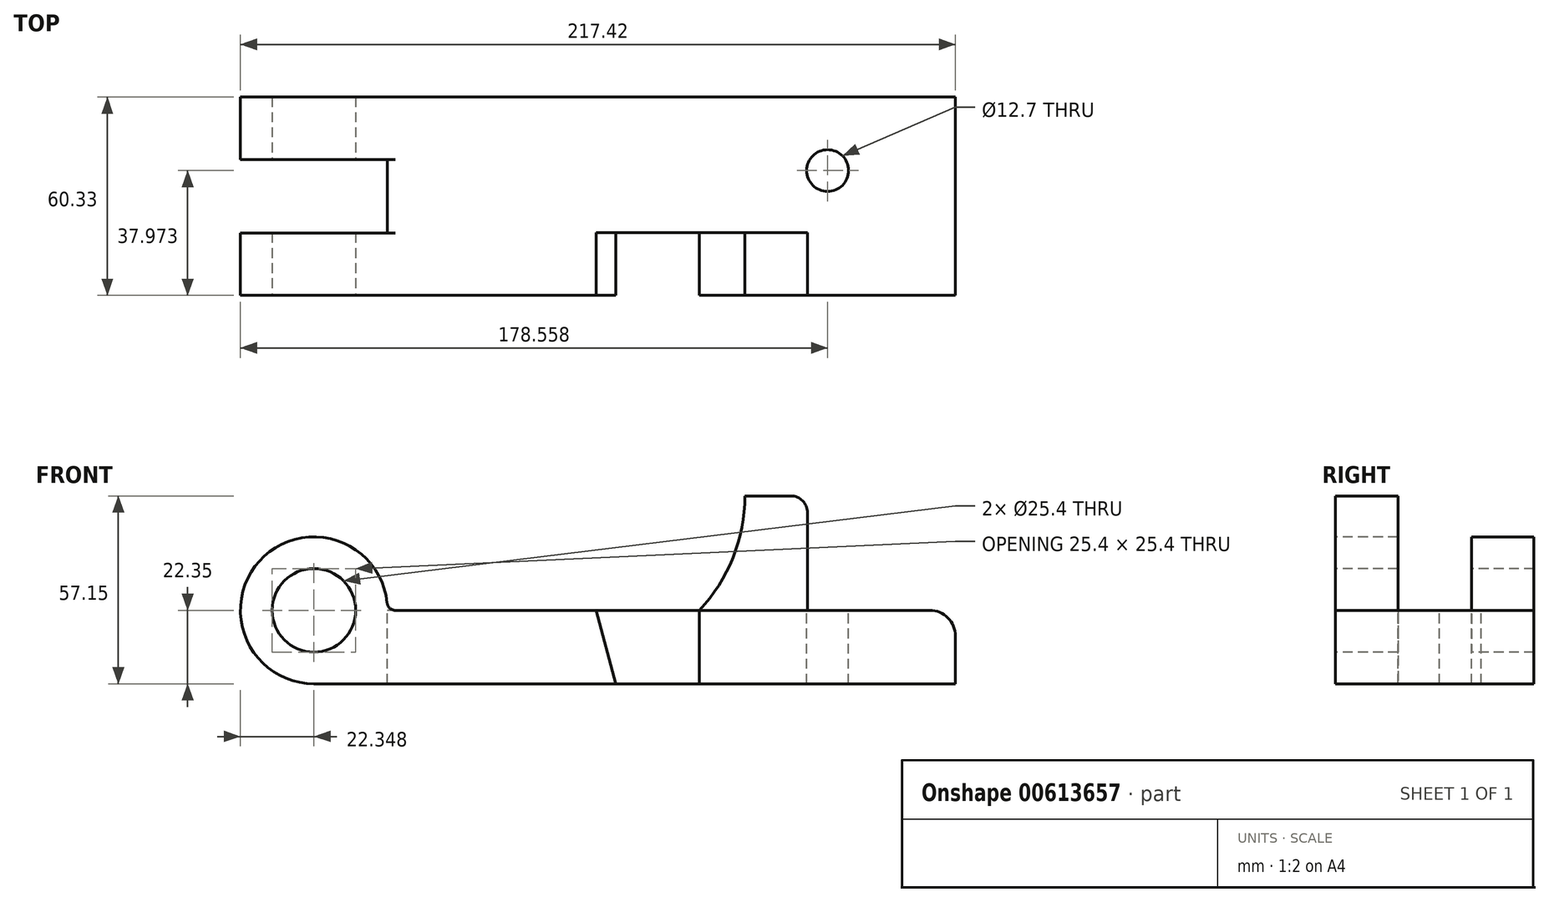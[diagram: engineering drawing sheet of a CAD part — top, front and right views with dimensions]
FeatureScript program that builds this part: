
annotation { "Feature Type Name" : "Feature", "Feature Type Description" : "" }
export const myFeature = defineFeature(function(context is Context, id is Id, definition is map)
    precondition{}
    {
        {
            var Q0;
            Q0=qCreatedBy(makeId("Front.planeOp"),FACE);
            var sketch = newSketch(context, id + "F0", { "sketchPlane" : qUnion([Q0])});
            skCircle(sketch, "E0", {"center": v(-195.07, 0) * mm, "radius": 12.7 * mm});
            skArc(sketch, "E1", {"start": v(-172.72, 0) * mm, "mid": v(-210.88, 15.8) * mm, "end": v(-195.07, -22.35) * mm});
            skLineSegment(sketch, "E2.bottom", {"start": v(-172.72, 0) * mm, "end": v(-77.83, 0) * mm});
            skLineSegment(sketch, "E2.top", {"start": v(-195.07, -22.35) * mm, "end": v(0, -22.35) * mm});
            skLineSegment(sketch, "E2.right", {"start": v(0, 0) * mm, "end": v(0, -22.35) * mm});
            skLineSegment(sketch, "E3", {"start": v(-44.98, 0) * mm, "end": v(-44.98, 34.8) * mm});
            skLineSegment(sketch, "E4", {"start": v(-44.98, 34.8) * mm, "end": v(-64.03, 34.8) * mm});
            skLineSegment(sketch, "E5.trimOffspring", {"start": v(-44.98, 0) * mm, "end": v(0, 0) * mm});
            skLineSegment(sketch, "E6", {"start": v(-77.83, 0) * mm, "end": v(-44.98, 0) * mm});
            skArc(sketch, "E7", {"start": v(-77.83, 0) * mm, "mid": v(-67.6, 16.08) * mm, "end": v(-64.03, 34.8) * mm});
            skSolve(sketch);
        }
        {
            var Q0;
            Q0=makeQuery(id+"F0.imprint","IMPRINT",FACE,{"disambiguationData":[TD([[makeQuery(id+"F0.imprint","IMPRINT",EDGE,{"derivedFrom":sQuery(id+"F0.wireOp",EDGE,"E0")}),-1.0]])]});
            extrude(context, id + "F1", {"entities" : qUnion([Q0]), "oppositeDirection" : true, "depth" : 60.32 * mm, "offsetDistance" : 25.4 * mm});
        }
        {
            var Q0;
            Q0=makeQuery(id+"F0.imprint","IMPRINT",FACE,{"disambiguationData":[TD([[makeQuery(id+"F0.imprint","IMPRINT",EDGE,{"derivedFrom":sQuery(id+"F0.wireOp",EDGE,"E3")}),1.0]])]});
            extrude(context, id + "F2", {"entities" : qUnion([Q0]), "oppositeDirection" : true, "depth" : 19.05 * mm, "offsetDistance" : 25.4 * mm});
        }
        {
            var Q0;
            Q0=makeQuery(id+"F0.imprint","IMPRINT",FACE,{"disambiguationData":[TD([[makeQuery(id+"F0.imprint","IMPRINT",EDGE,{"derivedFrom":sQuery(id+"F0.wireOp",EDGE,"E0")}),-1.0]])]});
            var sketch = newSketch(context, id + "F3", { "sketchPlane" : qUnion([Q0])});
            skLineSegment(sketch, "E8", {"start": v(-77.83, 0) * mm, "end": v(-109.22, 0) * mm});
            skLineSegment(sketch, "E9", {"start": v(-109.22, 0) * mm, "end": v(-103.23, -22.35) * mm});
            skLineSegment(sketch, "E10", {"start": v(-103.23, -22.35) * mm, "end": v(-77.83, -22.35) * mm});
            skLineSegment(sketch, "E11", {"start": v(-77.83, -22.35) * mm, "end": v(-77.83, 0) * mm});
            skSolve(sketch);
        }
        {
            var Q0;
            Q0 = qSketchRegion(id + "F3", true);
            extrude(context, id + "F4", {"entities" : qUnion([Q0]), "operationType" : NewBodyOperationType.REMOVE, "oppositeDirection" : true, "depth" : 19.05 * mm, "offsetDistance" : 25.4 * mm});
        }
        {
            var Q0;
            Q0=makeQuery(id+"F1.opExtrude","SWEPT_FACE",FACE,{"disambiguationData":[OSD([sQuery(id+"F0.wireOp",EDGE,"E2.bottom"),sQuery(id+"F0.wireOp",EDGE,"E5.trimOffspring"),sQuery(id+"F0.wireOp",EDGE,"E6")])]});
            var sketch = newSketch(context, id + "F5", { "sketchPlane" : qUnion([Q0])});
            skLineSegment(sketch, "E12.bottom", {"start": v(-172.72, 19) * mm, "end": v(-257.77, 19) * mm});
            skLineSegment(sketch, "E12.top", {"start": v(-172.72, 41.33) * mm, "end": v(-257.77, 41.33) * mm});
            skLineSegment(sketch, "E12.left", {"start": v(-172.72, 19) * mm, "end": v(-172.72, 41.33) * mm});
            skLineSegment(sketch, "E12.right", {"start": v(-257.77, 19) * mm, "end": v(-257.77, 41.33) * mm});
            skCircle(sketch, "E13", {"center": v(-38.86, 37.97) * mm, "radius": 6.35 * mm});
            skSolve(sketch);
        }
        {
            var Q0;
            Q0 = qSketchRegion(id + "F5", true);
            extrude(context, id + "F6", {"entities" : qUnion([Q0]), "operationType" : NewBodyOperationType.REMOVE, "endBound" : BoundingType.SYMMETRIC, "oppositeDirection" : true, "depth" : 58.93 * mm, "offsetDistance" : 25.4 * mm});
        }
        {
            var Q0;
            Q0=makeQuery(id+"F1.opExtrude","SWEPT_EDGE",EDGE,{"disambiguationData":[OSD([sQuery(id+"F0.wireOp",EDGE,"E2.right"),sQuery(id+"F0.wireOp",EDGE,"E5.trimOffspring")])]});
            fillet(context, id + "F7", {"entities" : qUnion([Q0]), "radius" : 7.87 * mm, "tangentPropagation" : true, "allowEdgeOverflow" : false});
        }
        {
            var Q0;
            Q0=makeQuery(id+"F2.opExtrude","SWEPT_EDGE",EDGE,{"disambiguationData":[OSD([sQuery(id+"F0.wireOp",EDGE,"E3"),sQuery(id+"F0.wireOp",EDGE,"E4")])]});
            fillet(context, id + "F8", {"entities" : qUnion([Q0]), "radius" : 5.08 * mm, "tangentPropagation" : true, "allowEdgeOverflow" : false});
        }
        {
            var Q0;
            {var subQ0=sQuery(id+"F0.wireOp",EDGE,"E6");var subQ1=sQuery(id+"F0.wireOp",EDGE,"E5.trimOffspring");var subQ2=sQuery(id+"F0.wireOp",EDGE,"E2.bottom");var subQ3=sQuery(id+"F0.wireOp",EDGE,"E1");var subQ4=makeQuery(id+"F1.opExtrude","SWEPT_FACE",FACE,{"disambiguationData":[OSD([subQ2,subQ1,subQ0])]});var subQ5=makeQuery(id+"F1.opExtrude","SWEPT_FACE",FACE,{"disambiguationData":[OSD([subQ3])]});Q0=makeQuery(id+"F6.boolean.opBoolean","SPLIT",EDGE,{"disambiguationData":[topologyDisambiguationEdgeConnected([subQ5,subQ4]),TD([makeQuery(id+"F6.opExtrude","SWEPT_FACE",FACE,{"disambiguationData":[OSD([sQuery(id+"F5.wireOp",EDGE,"E12.top")])]})])],"derivedFrom":makeQuery(id+"F1.opExtrude","SWEPT_EDGE",EDGE,{"disambiguationData":[OSD([subQ3,subQ2])]})});}
            var Q1;
            {var subQ0=sQuery(id+"F0.wireOp",EDGE,"E6");var subQ1=sQuery(id+"F0.wireOp",EDGE,"E5.trimOffspring");var subQ2=sQuery(id+"F0.wireOp",EDGE,"E2.bottom");var subQ3=makeQuery(id+"F1.opExtrude","SWEPT_FACE",FACE,{"disambiguationData":[OSD([subQ2,subQ1,subQ0])]});var subQ4=sQuery(id+"F0.wireOp",EDGE,"E1");var subQ5=makeQuery(id+"F1.opExtrude","SWEPT_FACE",FACE,{"disambiguationData":[OSD([subQ4])]});Q1=makeQuery(id+"F6.boolean.opBoolean","SPLIT",EDGE,{"disambiguationData":[topologyDisambiguationEdgeConnected([subQ5,subQ3]),TD([makeQuery(id+"F6.opExtrude","SWEPT_FACE",FACE,{"disambiguationData":[OSD([sQuery(id+"F5.wireOp",EDGE,"E12.bottom")])]})])],"derivedFrom":makeQuery(id+"F1.opExtrude","SWEPT_EDGE",EDGE,{"disambiguationData":[OSD([subQ4,subQ2])]})});}
            fillet(context, id + "F9", {"entities" : qUnion([Q0, Q1]), "radius" : 2.54 * mm, "tangentPropagation" : true, "allowEdgeOverflow" : false});
        }
    });
